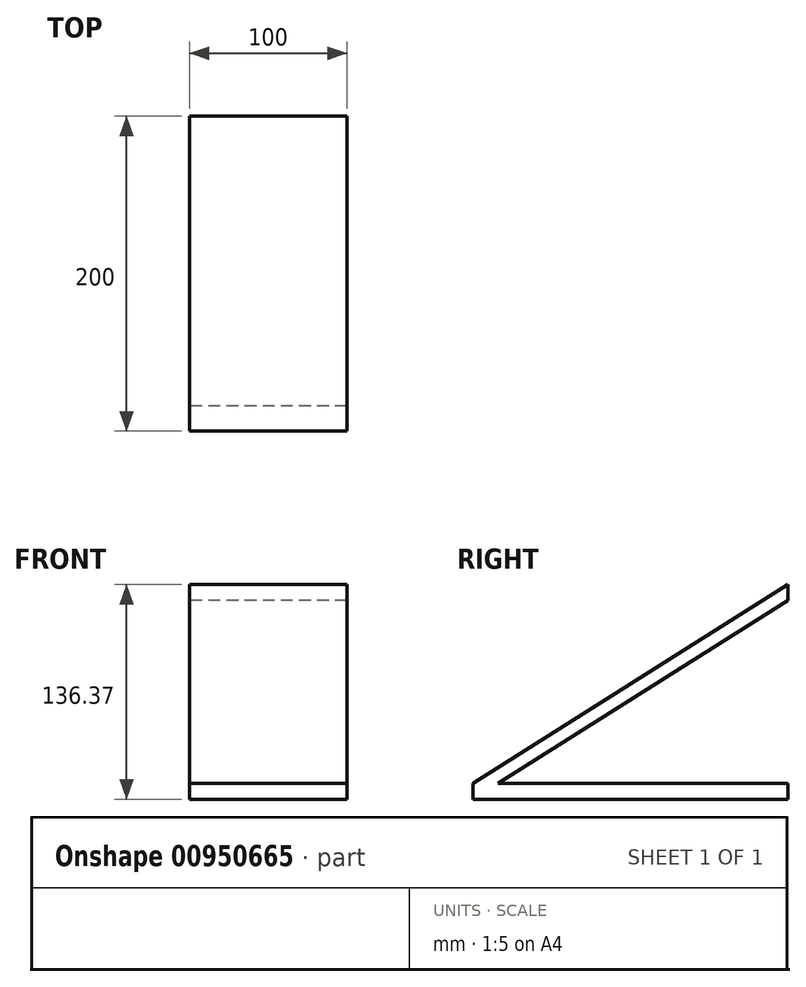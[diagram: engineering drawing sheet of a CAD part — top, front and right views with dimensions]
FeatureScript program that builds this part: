
annotation { "Feature Type Name" : "Feature", "Feature Type Description" : "" }
export const myFeature = defineFeature(function(context is Context, id is Id, definition is map)
    precondition{}
    {
        {
            var Q0;
            Q0=qCreatedBy(makeId("Right.planeOp"),FACE);
            var sketch = newSketch(context, id + "F0", { "sketchPlane" : qUnion([Q0])});
            skLineSegment(sketch, "E0.bottom", {"start": v(0, 0) * mm, "end": v(200, 0) * mm});
            skLineSegment(sketch, "E0.top", {"start": v(0, 10) * mm, "end": v(200, 10) * mm});
            skLineSegment(sketch, "E0.left", {"start": v(0, 0) * mm, "end": v(0, 10) * mm});
            skLineSegment(sketch, "E0.right", {"start": v(200, 0) * mm, "end": v(200, 10) * mm});
            skLineSegment(sketch, "E1", {"start": v(0, 0) * mm, "end": v(200, 126.37) * mm});
            skLineSegment(sketch, "E2", {"start": v(200, 10) * mm, "end": v(200, 173.09) * mm});
            skLineSegment(sketch, "E3", {"start": v(0, 10) * mm, "end": v(200, 136.37) * mm});
            skSolve(sketch);
        }
        {
            var Q0;
            {var subQ0=sQuery(id+"F0.wireOp",EDGE,"E3");Q0=makeQuery(id+"F0.imprint","IMPRINT",FACE,{"disambiguationData":[TD([[makeQuery(id+"F0.imprint","IMPRINT",EDGE,{"derivedFrom":subQ0}),-1.0]])]});}
            var Q1;
            {var subQ0=sQuery(id+"F0.wireOp",EDGE,"E0.left");Q1=makeQuery(id+"F0.imprint","IMPRINT",FACE,{"disambiguationData":[TD([[makeQuery(id+"F0.imprint","IMPRINT",EDGE,{"derivedFrom":subQ0}),-1.0]])]});}
            var Q2;
            {var subQ0=sQuery(id+"F0.wireOp",EDGE,"E0.bottom");Q2=makeQuery(id+"F0.imprint","IMPRINT",FACE,{"disambiguationData":[TD([[makeQuery(id+"F0.imprint","IMPRINT",EDGE,{"derivedFrom":subQ0}),1.0]])]});}
            extrude(context, id + "F1", {"entities" : qUnion([Q0, Q1, Q2]), "depth" : 100 * mm, "offsetDistance" : 25 * mm});
        }
    });
